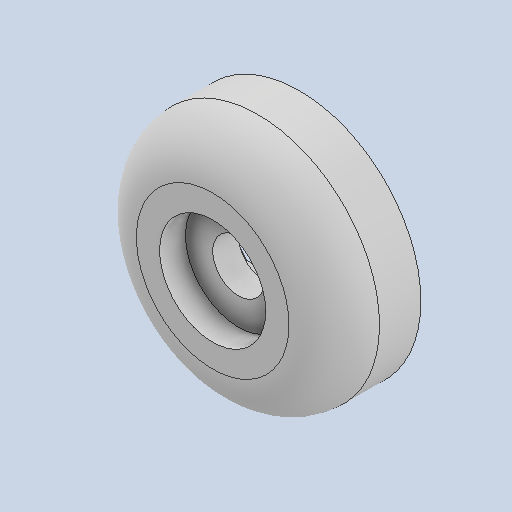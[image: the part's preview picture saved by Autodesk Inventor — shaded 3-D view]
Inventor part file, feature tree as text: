
AUTODESK INVENTOR PART (.ipt)
format: ipt  version: 2022 (Build 260153070, 153G)  size: 161,280 bytes
history: native  units: mm
features: reference x7, other x4, sketch x3, extrude x3, plane x1, fillet x1
ambient origin geometry x8: Origin, YZ Plane, XZ Plane, XY Plane, X Axis, Y Axis, Z Axis, Center Point
bodies: Solid1 (feature_tree)
feature tree (19):
  sketch  "Sketch1"  dims[d0=0.2mm d1=0.0mm d2=1.15mm d3=0.0mm]
  plane  "Work Plane1"
  extrude  "Extrusion1"  Depth=1.15mm TaperAngle=0.0deg
  extrude  "Extrusion2"  Depth=1.75mm
  fillet  "Fillet1"  Radius=4.1mm
  extrude  "Extrusion3"  [1 undecoded]
  reference  "Reference1"
  reference  "Reference2"
  reference  "Reference3"
  reference  "Reference4"
  reference  "Reference5"
  reference  "Reference6"
  sketch  "Sketch2"  dims[d4=2.0mm d5=0.0mm d6=1.75mm d7=4.1mm]
  reference  "Reference7"
  sketch  "Sketch3"  dims[d8=1.0mm d9=0.0mm]
  other  "<userpath> laptop\Desktop\SumoBot\sumobotENCODER\MotorEncoderAssembly.iam"
  other  "MotorEncoderAssembly.iam"
  other  "TTencoderspacer:1"
  other  "TT motor output:1"
note: 1 required parameter value undecoded (feature->parameter linkage not recoverable at this tier; creation-order binding heuristic only, values carry confidence <= 0.55)
